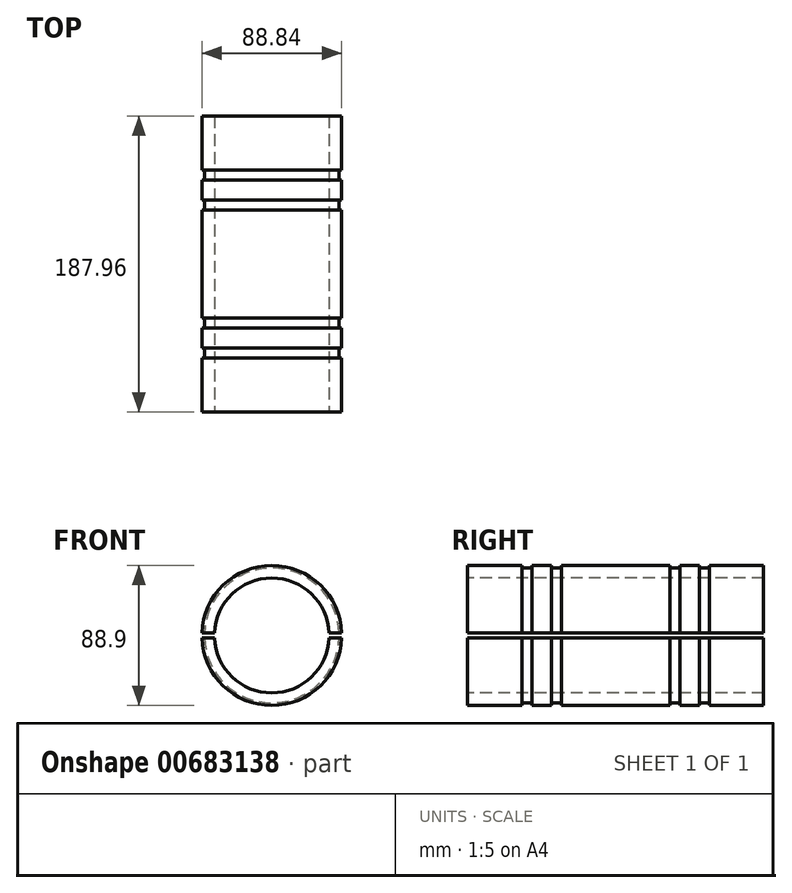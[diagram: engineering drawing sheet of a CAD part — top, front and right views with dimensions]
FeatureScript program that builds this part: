
annotation { "Feature Type Name" : "Feature", "Feature Type Description" : "" }
export const myFeature = defineFeature(function(context is Context, id is Id, definition is map)
    precondition{}
    {
        {
            var Q0;
            Q0=qCreatedBy(makeId("Front.planeOp"),FACE);
            var sketch = newSketch(context, id + "F0", { "sketchPlane" : qUnion([Q0])});
            skArc(sketch, "E0", {"start": v(-36.48, -1.59) * mm, "mid": v(0, -36.51) * mm, "end": v(36.48, -1.59) * mm});
            skArc(sketch, "E1", {"start": v(44.42, 1.59) * mm, "mid": v(0, 44.45) * mm, "end": v(-44.42, 1.59) * mm});
            skLineSegment(sketch, "E2", {"start": v(0, 0) * mm, "end": v(0, 44.45) * mm, "construction": true});
            skLineSegment(sketch, "E3", {"start": v(-44.45, 0) * mm, "end": v(0, 0) * mm, "construction": true});
            skLineSegment(sketch, "E4", {"start": v(-44.42, 1.59) * mm, "end": v(-36.48, 1.59) * mm});
            skLineSegment(sketch, "E5.MirrorCS", {"start": v(44.42, 1.59) * mm, "end": v(36.48, 1.59) * mm});
            skLineSegment(sketch, "E6.MirrorCS", {"start": v(-44.42, -1.59) * mm, "end": v(-36.48, -1.59) * mm});
            skLineSegment(sketch, "E7.MirrorCS", {"start": v(44.42, -1.59) * mm, "end": v(36.48, -1.59) * mm});
            skArc(sketch, "E8.trimOffspring", {"start": v(36.48, 1.59) * mm, "mid": v(0, 36.51) * mm, "end": v(-36.48, 1.59) * mm});
            skArc(sketch, "E9.trimOffspring", {"start": v(-44.42, -1.59) * mm, "mid": v(0, -44.45) * mm, "end": v(44.42, -1.59) * mm});
            skCircle(sketch, "E10", {"center": v(0, 0) * mm, "radius": 42.86 * mm, "construction": true});
            skSolve(sketch);
        }
        {
            var Q0;
            Q0 = qSketchRegion(id + "F0", true);
            extrude(context, id + "F1", {"entities" : qUnion([Q0]), "endBound" : BoundingType.SYMMETRIC, "oppositeDirection" : true, "depth" : 187.96 * mm, "offsetDistance" : 25.4 * mm});
        }
        {
            var Q0;
            Q0=qCreatedBy(makeId("Top.planeOp"),FACE);
            var sketch = newSketch(context, id + "F2", { "sketchPlane" : qUnion([Q0])});
            skLineSegment(sketch, "E11", {"start": v(0, 0) * mm, "end": v(-44.42, 0) * mm, "construction": true});
            skLineSegment(sketch, "E12", {"start": v(-44.42, 0) * mm, "end": v(-44.42, 47) * mm, "construction": true});
            skLineSegment(sketch, "E13", {"start": v(-44.42, 46.99) * mm, "end": v(0, 47) * mm, "construction": true});
            skLineSegment(sketch, "E14", {"start": v(0, 0) * mm, "end": v(0, 47) * mm, "construction": true});
            skLineSegment(sketch, "E15.bottom", {"start": v(-46, 53.21) * mm, "end": v(-42.83, 53.21) * mm, "construction": true});
            skLineSegment(sketch, "E15.top", {"start": v(-46, 40.77) * mm, "end": v(-42.83, 40.77) * mm, "construction": true});
            skLineSegment(sketch, "E15.left", {"start": v(-46, 53.21) * mm, "end": v(-46, 40.77) * mm, "construction": true});
            skLineSegment(sketch, "E15.right", {"start": v(-42.83, 53.21) * mm, "end": v(-42.83, 40.77) * mm, "construction": true});
            skPoint(sketch, "E15.middle", {"position": v(-44.42, 47) * mm});
            skLineSegment(sketch, "E16", {"start": v(-44.42, 47) * mm, "end": v(-44.42, 53.21) * mm, "construction": true});
            skLineSegment(sketch, "E17.bottom", {"start": v(-46, 53.21) * mm, "end": v(-42.83, 53.21) * mm});
            skLineSegment(sketch, "E17.top", {"start": v(-46, 59.56) * mm, "end": v(-42.83, 59.56) * mm});
            skLineSegment(sketch, "E17.left", {"start": v(-46, 53.21) * mm, "end": v(-46, 59.56) * mm});
            skLineSegment(sketch, "E17.right", {"start": v(-42.83, 53.21) * mm, "end": v(-42.83, 59.56) * mm});
            skLineSegment(sketch, "E18.MirrorCS", {"start": v(-46, 40.77) * mm, "end": v(-42.83, 40.77) * mm});
            skLineSegment(sketch, "E19.MirrorCS", {"start": v(-42.83, 40.77) * mm, "end": v(-42.83, 34.42) * mm});
            skLineSegment(sketch, "E20.MirrorCS", {"start": v(-46, 40.77) * mm, "end": v(-46, 34.42) * mm});
            skLineSegment(sketch, "E21.MirrorCS", {"start": v(-46, 34.42) * mm, "end": v(-42.83, 34.42) * mm});
            skLineSegment(sketch, "E22.MirrorCS", {"start": v(-46, -40.77) * mm, "end": v(-42.83, -40.77) * mm});
            skLineSegment(sketch, "E23.MirrorCS", {"start": v(-46, -40.77) * mm, "end": v(-42.83, -40.77) * mm, "construction": true});
            skLineSegment(sketch, "E24.MirrorCS", {"start": v(-46, -34.42) * mm, "end": v(-42.83, -34.42) * mm});
            skLineSegment(sketch, "E25.MirrorCS", {"start": v(-46, -40.77) * mm, "end": v(-46, -34.42) * mm});
            skLineSegment(sketch, "E26.MirrorCS", {"start": v(-42.83, -40.77) * mm, "end": v(-42.83, -34.42) * mm});
            skLineSegment(sketch, "E27.MirrorCS", {"start": v(-46, -53.21) * mm, "end": v(-42.83, -53.21) * mm});
            skLineSegment(sketch, "E28.MirrorCS", {"start": v(-46, -53.21) * mm, "end": v(-42.83, -53.21) * mm, "construction": true});
            skLineSegment(sketch, "E29.MirrorCS", {"start": v(-42.83, -53.21) * mm, "end": v(-42.83, -59.56) * mm});
            skLineSegment(sketch, "E30.MirrorCS", {"start": v(-46, -59.56) * mm, "end": v(-42.83, -59.56) * mm});
            skLineSegment(sketch, "E31.MirrorCS", {"start": v(-46, -53.21) * mm, "end": v(-46, -59.56) * mm});
            skSolve(sketch);
        }
        {
            var Q0;
            Q0 = qSketchRegion(id + "F2", true);
            var Q1;
            Q1=sQuery(id+"F2.wireOp",EDGE,"E14");
            revolve(context, id + "F3", {"operationType" : NewBodyOperationType.REMOVE, "entities" : qUnion([Q0]), "axis" : qUnion([Q1]), "revolveType" : RevolveType.FULL, "oppositeDirection" : true});
        }
    });
